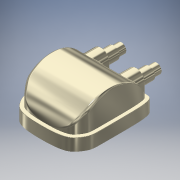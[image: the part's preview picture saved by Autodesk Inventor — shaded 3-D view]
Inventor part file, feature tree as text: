
AUTODESK INVENTOR PART (.ipt)
format: ipt  version: 2016 (Build 200138000, 138)  size: 914,944 bytes
history: native  units: in
note: dims shown in document units (in); Inventor stores cm internally (conversion verified against a paired STEP export)
features: extrude x16, sketch x16, projected_geometry x16, fillet x9, mirror x3, plane x2, hole x2
ambient origin geometry x8: Origin, YZ Plane, XZ Plane, XY Plane, X Axis, Y Axis, Z Axis, Center Point
bodies: Solid1 (feature_tree)
feature tree (64):
  extrude  "Extrusion1"  Depth=3.5433in
  extrude  "Extrusion2"  Depth=0.1575in
  extrude  "Extrusion3"  Depth=1.2402in TaperAngle=0.0deg
  extrude  "Extrusion5"  Depth=0.748in
  mirror  "Mirror3"
  fillet  "Fillet8"  Radius=0.8661in
  fillet  "Fillet9"  Radius=1.6929in
  fillet  "Fillet10"  [1 undecoded]
  extrude  "Extrusion6"  Depth=0.1969in
  extrude  "Extrusion7"  Depth=0.063in
  extrude  "Extrusion8"  Depth=0.5512in
  mirror  "Mirror4"
  extrude  "Extrusion9"  Depth=0.3937in TaperAngle=0.0deg
  extrude  "Extrusion10"  Depth=0.3543in TaperAngle=0.0deg
  plane  "Work Plane2"
  extrude  "Extrusion11"  Depth=0.0787in TaperAngle=0.0deg
  extrude  "Extrusion12"  Depth=0.5906in
  fillet  "Fillet11"  Radius=0.7874in
  hole  "Hole2"  [1 undecoded]
  sketch  "Sketch16"  dims[d58=0.2559in d59=0.0in d60=1.5748in]
  extrude  "Extrusion13"  Depth=1.5748in
  extrude  "Extrusion14"  Depth=0.3543in
  extrude  "Extrusion15"  Depth=0.1181in
  hole  "Hole3"  [1 undecoded]
  fillet  "Fillet12"  Radius=2.3622in
  fillet  "Fillet13"  Radius=2.3622in
  fillet  "Fillet14"  Radius=0.0394in
  fillet  "Fillet15"  Radius=0.0787in
  extrude  "Extrusion16"  Depth=0.0157in
  extrude  "Extrusion17"  Depth=0.0787in
  fillet  "Fillet16"  Radius=0.0787in
  mirror  "Mirror5"
  plane  "Work Plane3"
  sketch  "Sketch1"  dims[d0=3.0709in d1=3.5433in]
  sketch  "Sketch2"  dims[d2=0.5512in d3=0.0in d4=0.1575in]
  projected_geometry  "Projected Loop2"
  sketch  "Sketch4"  dims[d5=1.378in d6=0.0in d7=1.2402in d8=0.0in]
  projected_geometry  "Projected Loop3"
  sketch  "Sketch5"  dims[d20=1.5748in d31=0.748in d33=0.8661in d34=1.6929in d35=0.0in d36=0.0in]
  sketch  "Sketch7"  dims[d37=0.1969in d38=0.1969in]
  sketch  "Sketch8"  dims[d39=0.0in d40=0.063in]
  sketch  "Sketch9"  dims[d41=0.063in d42=0.5512in]
  sketch  "Sketch10"  dims[d43=0.3937in d44=0.5512in d45=0.0in]
  sketch  "Sketch11"  dims[d46=0.0591in d47=0.3543in d48=0.0in]
  projected_geometry  "Projected Loop4"
  sketch  "Sketch12"  dims[d49=0.0787in d50=0.7874in d51=0.0in]
  projected_geometry  "Projected Loop5"
  sketch  "Sketch14"  dims[d52=1.811in d53=0.5906in d54=0.7874in d55=0.0in]
  sketch  "Sketch15"  dims[d56=1.9685in d57=1.9685in]
  projected_geometry  "Projected Loop10"
  projected_geometry  "Projected Loop11"
  sketch  "Sketch17"  dims[d61=1.5748in d62=0.3543in]
  projected_geometry  "Projected Loop12"
  projected_geometry  "Projected Loop13"
  projected_geometry  "Projected Loop14"
  projected_geometry  "Projected Loop15"
  sketch  "Sketch18"  dims[d63=0.1476in d64=0.0in d72=0.1181in]
  sketch  "Sketch20"  dims[d73=0.0906in d74=0.0in d75=0.1969in d76=2.3622in d77=2.3622in d78=0.1181in d79=0.2362in d80=0.1575in d81=0.0787in d82=90.0deg d83=0.4724in d84=0.8108in d85=0.0394in d86=0.0787in d87=0.0in d88=0.1181in d89=0.0787in d90=0.0787in d91=0.0787in d92=0.0787in d93=0.4547in d94=0.0in d95=0.0787in d96=0.0in d98=-0.0512in d99=0.1181in d100=0.2362in d101=0.1575in d102=0.0787in d103=90.0deg d104=0.3937in d105=0.8108in d106=0.0197in d107=0.0197in d108=0.0157in d109=0.0157in d110=0.0787in d111=0.6299in d112=1.1417in d113=0.6406in d114=0.0in d116=0.0236in d117=0.0787in d118=0.0394in d119=0.4134in d120=0.0in d121=0.0157in d122=-0.4921in]
  projected_geometry  "Projected Loop16"
  projected_geometry  "Project Cut Edges3"
  projected_geometry  "Project Cut Edges4"
  projected_geometry  "Project Cut Edges5"
  projected_geometry  "Project Cut Edges6"
  projected_geometry  "Project Cut Edges7"
note: 3 required parameter values undecoded (feature->parameter linkage not recoverable at this tier; creation-order binding heuristic only, values carry confidence <= 0.55)
